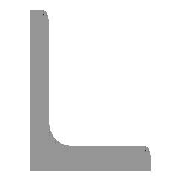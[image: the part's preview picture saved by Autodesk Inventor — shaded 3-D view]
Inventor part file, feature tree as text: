
AUTODESK INVENTOR PART (.ipt)
format: ipt  version: 2024.1 (Build 281209000, 209)  size: 121,344 bytes
history: native  units: mm (DEFAULTED — no unit token found)
features: other x4, sketch x1, plane x1
ambient origin geometry x8: Origin, YZ Plane, XZ Plane, XY Plane, X Axis, Y Axis, Z Axis, Center Point
bodies: Solid1 (feature_tree), Body (feature_tree)
feature tree (6):
  parser-record x1  (decoder bookkeeping rows leaked as tree rows — omitted from the tree; the rows remain in map.json)
  other  "Driven Length"
  other  "Start Plane"
  other  "End Plane"
  sketch  "Sketch3"  dims[d0=25.4mm d1=25.4mm d2=3.175mm d3=3.175mm d4=1200.0mm d5=0.0mm d10=0.0mm d11=0.0mm d12=-0.0mm d13=1200.0mm d14=3.302mm d15=1.524mm d16=90.0deg d17=1200.0mm]
  plane  "Work Plane3"
